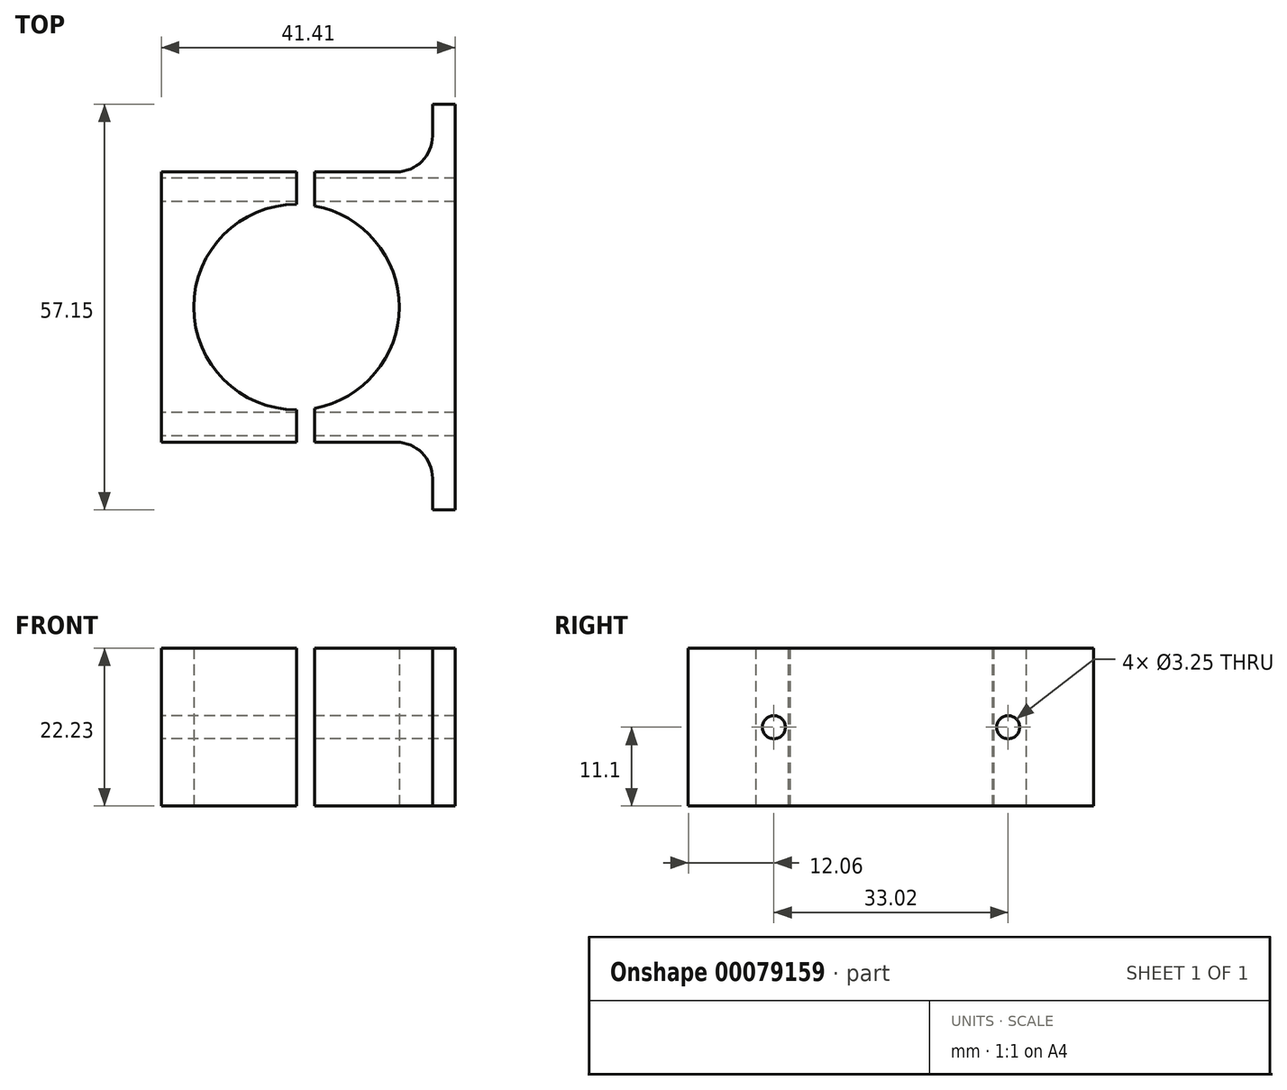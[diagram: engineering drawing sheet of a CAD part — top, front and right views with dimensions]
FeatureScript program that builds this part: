
annotation { "Feature Type Name" : "Feature", "Feature Type Description" : "" }
export const myFeature = defineFeature(function(context is Context, id is Id, definition is map)
    precondition{}
    {
        {
            var Q0;
            Q0=qCreatedBy(makeId("Top.planeOp"),FACE);
            var sketch = newSketch(context, id + "F0", { "sketchPlane" : qUnion([Q0])});
            skLineSegment(sketch, "E0.bottom", {"start": v(6.73, -19.05) * mm, "end": v(-9.9, -19.05) * mm});
            skLineSegment(sketch, "E0.top", {"start": v(6.73, 19.05) * mm, "end": v(-9.9, 19.05) * mm});
            skLineSegment(sketch, "E0.left", {"start": v(9.9, -19.05) * mm, "end": v(9.9, 19.05) * mm});
            skLineSegment(sketch, "E0.right", {"start": v(-9.9, -19.05) * mm, "end": v(-9.9, -14.25) * mm});
            skPoint(sketch, "E0.middle", {"position": v(0, 0) * mm});
            skArc(sketch, "E1", {"start": v(-9.9, -14.25) * mm, "mid": v(2.03, 0) * mm, "end": v(-9.9, 14.25) * mm});
            skLineSegment(sketch, "E2.trimOffspring", {"start": v(-9.9, 14.25) * mm, "end": v(-9.9, 19.05) * mm});
            skLineSegment(sketch, "E3.top", {"start": v(9.9, -28.57) * mm, "end": v(6.73, -28.57) * mm});
            skLineSegment(sketch, "E3.left", {"start": v(9.9, -19.05) * mm, "end": v(9.9, -28.57) * mm});
            skLineSegment(sketch, "E3.right", {"start": v(6.73, -19.05) * mm, "end": v(6.73, -28.57) * mm});
            skLineSegment(sketch, "E4.top", {"start": v(9.9, 28.58) * mm, "end": v(6.73, 28.58) * mm});
            skLineSegment(sketch, "E4.left", {"start": v(9.9, 19.05) * mm, "end": v(9.9, 28.58) * mm});
            skLineSegment(sketch, "E4.right", {"start": v(6.73, 19.05) * mm, "end": v(6.73, 28.58) * mm});
            skLineSegment(sketch, "E5", {"start": v(-12.45, 14.48) * mm, "end": v(-12.45, 19.05) * mm});
            skLineSegment(sketch, "E6", {"start": v(-12.45, 19.05) * mm, "end": v(-31.5, 19.05) * mm});
            skLineSegment(sketch, "E7", {"start": v(-31.5, 19.05) * mm, "end": v(-31.5, -19.05) * mm});
            skLineSegment(sketch, "E8", {"start": v(-31.5, -19.05) * mm, "end": v(-12.45, -19.05) * mm});
            skLineSegment(sketch, "E9", {"start": v(-12.45, -19.05) * mm, "end": v(-12.45, -14.48) * mm});
            skArc(sketch, "E10", {"start": v(-12.45, 14.48) * mm, "mid": v(-26.92, 0) * mm, "end": v(-12.45, -14.48) * mm});
            skSolve(sketch);
        }
        {
            var Q0;
            Q0 = qSketchRegion(id + "F0", true);
            extrude(context, id + "F1", {"entities" : qUnion([Q0]), "depth" : 22.22 * mm});
        }
        {
            var Q0;
            Q0=makeQuery(id+"F1.opExtrude","SWEPT_FACE",FACE,{"disambiguationData":[OSD([sQuery(id+"F0.wireOp",EDGE,"E0.left")])]});
            var sketch = newSketch(context, id + "F2", { "sketchPlane" : qUnion([Q0])});
            skCircle(sketch, "E11", {"center": v(16.51, 11.11) * mm, "radius": 1.13 * mm});
            skCircle(sketch, "E12", {"center": v(-16.51, 11.11) * mm, "radius": 1.13 * mm});
            skSolve(sketch);
        }
        {
            var Q0;
            Q0 = qSketchRegion(id + "F2", true);
            extrude(context, id + "F3", {"entities" : qUnion([Q0]), "operationType" : NewBodyOperationType.REMOVE, "endBound" : BoundingType.THROUGH_ALL, "oppositeDirection" : true, "offsetDistance" : 25.4 * mm, "depth" : 76.2 * mm});
        }
        {
            var Q0;
            Q0=makeQuery(id+"F1.opExtrude","SWEPT_EDGE",EDGE,{"disambiguationData":[OSD([sQuery(id+"F0.wireOp",EDGE,"E0.bottom"),sQuery(id+"F0.wireOp",EDGE,"E3.right")])]});
            var Q1;
            Q1=makeQuery(id+"F1.opExtrude","SWEPT_EDGE",EDGE,{"disambiguationData":[OSD([sQuery(id+"F0.wireOp",EDGE,"E0.top"),sQuery(id+"F0.wireOp",EDGE,"E4.right")])]});
            fillet(context, id + "F4", {"entities" : qUnion([Q0, Q1]), "radius" : 5.08 * mm, "tangentPropagation" : true, "allowEdgeOverflow" : false});
        }
        {
            var Q0;
            Q0=makeQuery(id+"F1.opExtrude","SWEPT_FACE",FACE,{"disambiguationData":[OSD([sQuery(id+"F0.wireOp",EDGE,"E7")])]});
            var sketch = newSketch(context, id + "F5", { "sketchPlane" : qUnion([Q0])});
            skCircle(sketch, "E13", {"center": v(16.51, 11.1) * mm, "radius": 1.63 * mm});
            skCircle(sketch, "E14", {"center": v(-16.51, 11.1) * mm, "radius": 1.63 * mm});
            skSolve(sketch);
        }
        {
            var Q0;
            Q0 = qSketchRegion(id + "F5", true);
            extrude(context, id + "F6", {"entities" : qUnion([Q0]), "operationType" : NewBodyOperationType.REMOVE, "endBound" : BoundingType.THROUGH_ALL, "oppositeDirection" : true, "depth" : 25.4 * mm, "offsetDistance" : 25.4 * mm});
        }
    });
